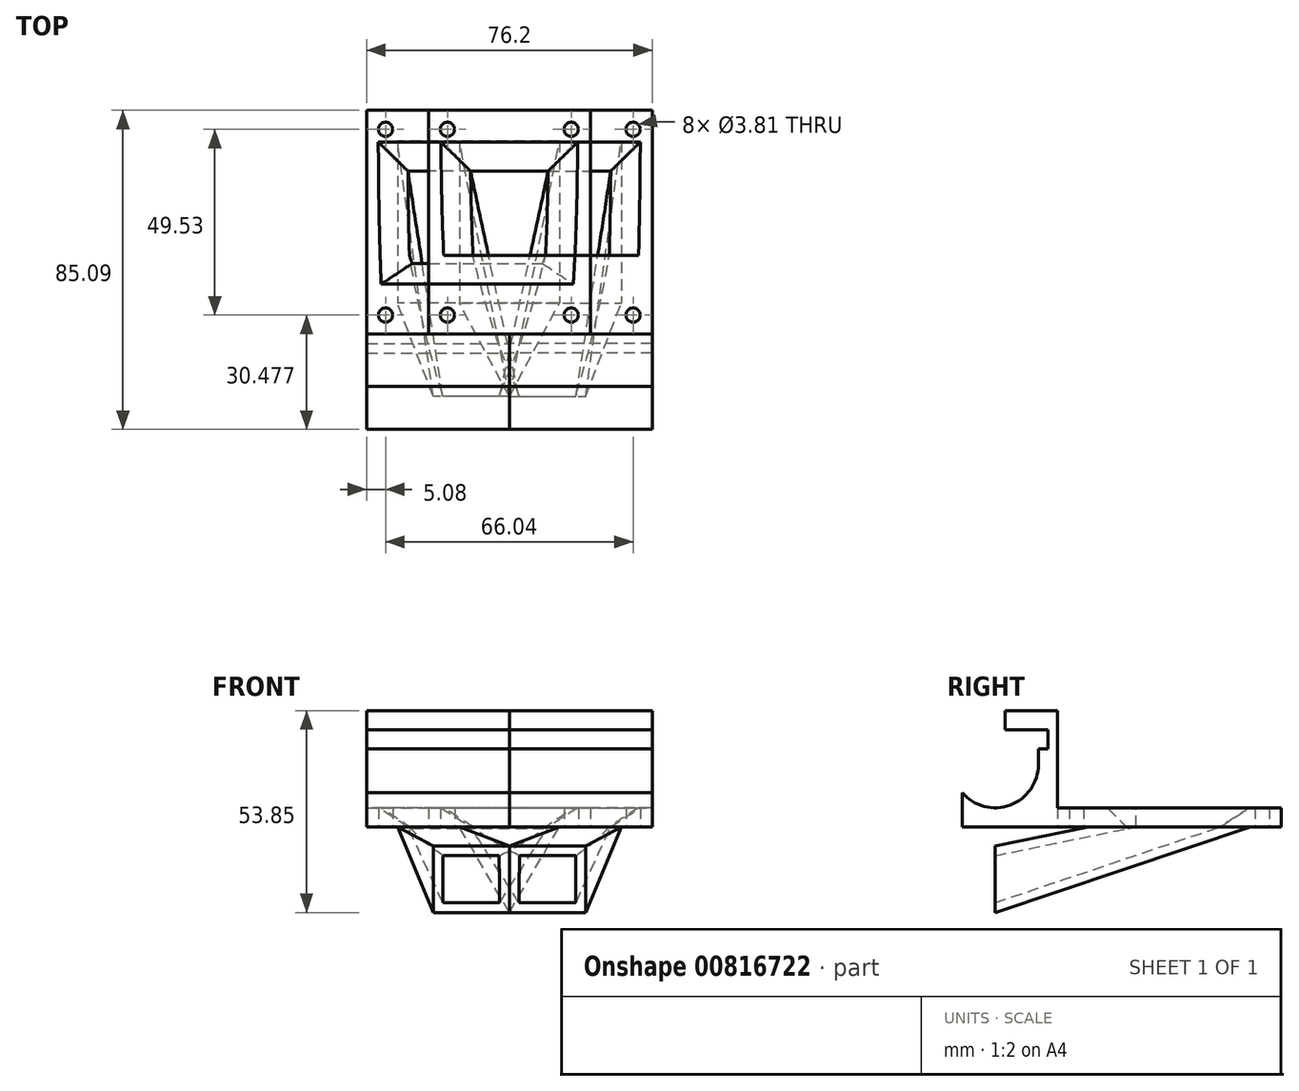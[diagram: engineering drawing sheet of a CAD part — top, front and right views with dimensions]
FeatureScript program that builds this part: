
annotation { "Feature Type Name" : "Feature", "Feature Type Description" : "" }
export const myFeature = defineFeature(function(context is Context, id is Id, definition is map)
    precondition{}
    {
        {
            var Q0;
            Q0=qCreatedBy(makeId("Right.planeOp"),FACE);
            var sketch = newSketch(context, id + "F0", { "sketchPlane" : qUnion([Q0])});
            skArc(sketch, "E0", {"start": v(-8.76, -7.53) * mm, "mid": v(4.02, -10.84) * mm, "end": v(11.56, 0) * mm});
            skLineSegment(sketch, "E1", {"start": v(-8.76, -7.53) * mm, "end": v(-8.76, -16.64) * mm});
            skLineSegment(sketch, "E2", {"start": v(-8.76, -16.64) * mm, "end": v(11.56, -16.64) * mm});
            skLineSegment(sketch, "E3", {"start": v(11.56, 0) * mm, "end": v(11.56, 4.2) * mm});
            skLineSegment(sketch, "E4", {"start": v(11.56, 4.2) * mm, "end": v(14.1, 4.2) * mm});
            skLineSegment(sketch, "E5", {"start": v(14.1, 4.2) * mm, "end": v(14.1, 9.27) * mm});
            skLineSegment(sketch, "E6", {"start": v(14.1, 9.27) * mm, "end": v(11.56, 9.27) * mm});
            skLineSegment(sketch, "E7", {"start": v(11.56, 9.27) * mm, "end": v(2.67, 9.27) * mm});
            skLineSegment(sketch, "E8", {"start": v(2.67, 9.27) * mm, "end": v(2.67, 14.35) * mm});
            skLineSegment(sketch, "E9", {"start": v(2.67, 14.35) * mm, "end": v(16.64, 14.35) * mm});
            skLineSegment(sketch, "E10", {"start": v(16.64, 14.35) * mm, "end": v(16.64, -16.64) * mm});
            skLineSegment(sketch, "E11", {"start": v(16.64, -16.64) * mm, "end": v(11.56, -16.64) * mm});
            skSolve(sketch);
        }
        {
            var Q0;
            Q0=makeQuery(id+"F0.imprint","IMPRINT",FACE,{"disambiguationData":[TD([[makeQuery(id+"F0.imprint","IMPRINT",EDGE,{"derivedFrom":sQuery(id+"F0.wireOp",EDGE,"E0")}),-1.0]])]});
            extrude(context, id + "F1", {"entities" : qUnion([Q0]), "depth" : 38.1 * mm, "offsetDistance" : 25.4 * mm});
        }
        {
            var Q0;
            Q0=makeQuery(id+"F1.opExtrude","SWEPT_FACE",FACE,{"disambiguationData":[OSD([sQuery(id+"F0.wireOp",EDGE,"E2"),sQuery(id+"F0.wireOp",EDGE,"E11")])]});
            var sketch = newSketch(context, id + "F2", { "sketchPlane" : qUnion([Q0])});
            skLineSegment(sketch, "E12", {"start": v(0, -16.64) * mm, "end": v(-21.6, -16.64) * mm});
            skLineSegment(sketch, "E13", {"start": v(-21.6, -16.64) * mm, "end": v(-21.59, -76.33) * mm});
            skLineSegment(sketch, "E14", {"start": v(-21.59, -76.33) * mm, "end": v(38.1, -76.33) * mm});
            skLineSegment(sketch, "E15", {"start": v(38.1, -76.33) * mm, "end": v(38.1, -16.64) * mm});
            skCircle(sketch, "E16", {"center": v(33.02, -71.25) * mm, "radius": 1.9 * mm});
            skCircle(sketch, "E17.0.1.0", {"center": v(33.02, -21.72) * mm, "radius": 1.9 * mm});
            skCircle(sketch, "E17.1.0.0", {"center": v(-16.51, -71.25) * mm, "radius": 1.9 * mm});
            skCircle(sketch, "E17.1.1.0", {"center": v(-16.51, -21.72) * mm, "radius": 1.9 * mm});
            skLineSegment(sketch, "E17.direction1", {"start": v(33.02, -71.25) * mm, "end": v(-16.51, -71.25) * mm, "construction": true});
            skLineSegment(sketch, "E17.direction2", {"start": v(33.02, -71.25) * mm, "end": v(33.02, -21.72) * mm, "construction": true});
            skPoint(sketch, "E18.top.end.orphan", {"position": v(0, -24.9) * mm});
            skLineSegment(sketch, "E19.bottom", {"start": v(-13.33, -68.07) * mm, "end": v(29.85, -68.07) * mm});
            skLineSegment(sketch, "E19.top", {"start": v(-13.34, -24.9) * mm, "end": v(29.84, -24.9) * mm});
            skLineSegment(sketch, "E19.left", {"start": v(-13.33, -68.07) * mm, "end": v(-13.34, -24.9) * mm});
            skLineSegment(sketch, "E19.right", {"start": v(29.85, -68.07) * mm, "end": v(29.84, -24.9) * mm});
            skSolve(sketch);
        }
        {
            var Q0;
            Q0=makeQuery(id+"F2.imprint","IMPRINT",FACE,{"disambiguationData":[TD([[makeQuery(id+"F2.imprint","IMPRINT",EDGE,{"derivedFrom":sQuery(id+"F2.wireOp",EDGE,"E12")}),1.0]])]});
            extrude(context, id + "F3", {"entities" : qUnion([Q0]), "operationType" : NewBodyOperationType.ADD, "oppositeDirection" : true, "depth" : 5.08 * mm, "offsetDistance" : 25.4 * mm});
        }
        {
            var Q0;
            Q0=qCreatedBy(makeId("Front.planeOp"),FACE);
            var sketch = newSketch(context, id + "F4", { "sketchPlane" : qUnion([Q0])});
            skLineSegment(sketch, "E20.bottom", {"start": v(0, -21.72) * mm, "end": v(20.32, -21.72) * mm});
            skLineSegment(sketch, "E20.top", {"start": v(0, -39.5) * mm, "end": v(20.32, -39.5) * mm});
            skLineSegment(sketch, "E20.left", {"start": v(0, -21.72) * mm, "end": v(0, -39.5) * mm});
            skLineSegment(sketch, "E20.right", {"start": v(20.32, -21.72) * mm, "end": v(20.32, -39.5) * mm});
            skSolve(sketch);
        }
        {
            var Q0;
            {var subQ0=sQuery(id+"F0.wireOp",EDGE,"E11");Q0=makeQuery(id+"F3.boolean.opBoolean","MERGE",FACE,{"derivedFrom":[makeQuery(id+"F1.opExtrude","SWEPT_FACE",FACE,{"disambiguationData":[OSD([sQuery(id+"F0.wireOp",EDGE,"E2"),subQ0])]}),makeQuery(id+"F3.opExtrude","CAP_FACE",FACE,{"disambiguationData":[OSD([sQuery(id+"F0.wireOp",EDGE,"E10"),subQ0,sQuery(id+"F2.wireOp",EDGE,"E12"),sQuery(id+"F2.wireOp",EDGE,"E13"),sQuery(id+"F2.wireOp",EDGE,"E14"),sQuery(id+"F2.wireOp",EDGE,"E15"),sQuery(id+"F2.wireOp",EDGE,"E16"),sQuery(id+"F2.wireOp",EDGE,"E17.0.1.0"),sQuery(id+"F2.wireOp",EDGE,"E17.1.0.0"),sQuery(id+"F2.wireOp",EDGE,"E17.1.1.0"),sQuery(id+"F2.wireOp",EDGE,"E19.bottom"),sQuery(id+"F2.wireOp",EDGE,"E19.top"),sQuery(id+"F2.wireOp",EDGE,"E19.left"),sQuery(id+"F2.wireOp",EDGE,"E19.right")])],"isStart":true})]});}
            var sketch = newSketch(context, id + "F5", { "sketchPlane" : qUnion([Q0])});
            skLineSegment(sketch, "E21.bottom", {"start": v(-24.13, -14.1) * mm, "end": v(40.64, -14.1) * mm});
            skLineSegment(sketch, "E21.top", {"start": v(-24.13, -78.87) * mm, "end": v(40.64, -78.87) * mm});
            skLineSegment(sketch, "E21.left", {"start": v(-24.13, -14.1) * mm, "end": v(-24.13, -78.87) * mm});
            skLineSegment(sketch, "E21.right", {"start": v(40.64, -14.1) * mm, "end": v(40.64, -78.87) * mm});
            skSolve(sketch);
        }
        {
            var Q0;
            Q0=makeQuery(id+"F4.imprint","IMPRINT",FACE,{"disambiguationData":[TD([[makeQuery(id+"F4.imprint","IMPRINT",EDGE,{"derivedFrom":sQuery(id+"F4.wireOp",EDGE,"E20.bottom")}),-1.0]])]});
            var Q1;
            Q1=makeQuery(id+"F5.imprint","IMPRINT",FACE,{"disambiguationData":[TD([[makeQuery(id+"F5.imprint","IMPRINT",EDGE,{"derivedFrom":makeQuery(id+"F3.opExtrude","CAP_EDGE",EDGE,{"disambiguationData":[OSD([sQuery(id+"F2.wireOp",EDGE,"E19.bottom")])],"isStart":true})}),1.0]])]});
            loft(context, id + "F6", {"sheetProfilesArray" : [{ "sheetProfileEntities" : qUnion([Q0]) }, { "sheetProfileEntities" : qUnion([Q1]) }]});
        }
        {
            var Q0;
            Q0=makeQuery(id+"F6.opLoft","CAP_FACE",FACE,{"disambiguationData":[OSD([makeQuery(id+"F5.imprint","IMPRINT",FACE,{"disambiguationData":[TD([[makeQuery(id+"F5.imprint","IMPRINT",EDGE,{"derivedFrom":makeQuery(id+"F3.opExtrude","CAP_EDGE",EDGE,{"disambiguationData":[OSD([sQuery(id+"F2.wireOp",EDGE,"E19.bottom")])],"isStart":true})}),1.0]])]})])],"isStart":true});
            var Q1;
            Q1=makeQuery(id+"F6.opLoft","CAP_FACE",FACE,{"disambiguationData":[OSD([makeQuery(id+"F4.imprint","IMPRINT",FACE,{"disambiguationData":[TD([[makeQuery(id+"F4.imprint","IMPRINT",EDGE,{"derivedFrom":sQuery(id+"F4.wireOp",EDGE,"E20.bottom")}),-1.0]])]})])],"isStart":true});
            shell(context, id + "F7", {"entities" : qUnion([Q0, Q1]), "thickness" : 2.54 * mm});
        }
        {
            var Q0;
            Q0=makeQuery(id+"F6.opLoft","CAP_FACE",FACE,{"disambiguationData":[OSD([makeQuery(id+"F5.imprint","IMPRINT",FACE,{"disambiguationData":[TD([[makeQuery(id+"F5.imprint","IMPRINT",EDGE,{"derivedFrom":makeQuery(id+"F3.opExtrude","CAP_EDGE",EDGE,{"disambiguationData":[OSD([sQuery(id+"F2.wireOp",EDGE,"E19.bottom")])],"isStart":true})}),1.0]])]})])],"isStart":true});
            extrude(context, id + "F8", {"entities" : qUnion([Q0]), "operationType" : NewBodyOperationType.ADD, "depth" : 5.08 * mm, "offsetDistance" : 25.4 * mm});
        }
        {
            var Q0;
            {var subQ0=sQuery(id+"F2.wireOp",EDGE,"E19.left");var subQ1=sQuery(id+"F2.wireOp",EDGE,"E19.top");var subQ2=sQuery(id+"F2.wireOp",EDGE,"E19.bottom");Q0=makeQuery(id+"F8.opExtrude","CAP_EDGE",EDGE,{"disambiguationData":[OSD([subQ2,subQ1,subQ0]),TDD([makeQuery(id+"F7.opShell","OFFSET_EDGE",EDGE,{"disambiguationData":[OSD([subQ2,subQ1,subQ0])]})])],"isStart":false});}
            var Q1;
            {var subQ0=sQuery(id+"F2.wireOp",EDGE,"E19.right");var subQ1=sQuery(id+"F2.wireOp",EDGE,"E19.left");var subQ2=sQuery(id+"F2.wireOp",EDGE,"E19.bottom");Q1=makeQuery(id+"F8.opExtrude","CAP_EDGE",EDGE,{"disambiguationData":[OSD([subQ2,subQ1,subQ0]),TDD([makeQuery(id+"F7.opShell","OFFSET_EDGE",EDGE,{"disambiguationData":[OSD([subQ2,subQ1,subQ0])]})])],"isStart":false});}
            var Q2;
            {var subQ0=sQuery(id+"F2.wireOp",EDGE,"E19.right");var subQ1=sQuery(id+"F2.wireOp",EDGE,"E19.top");var subQ2=sQuery(id+"F2.wireOp",EDGE,"E19.bottom");Q2=makeQuery(id+"F8.opExtrude","CAP_EDGE",EDGE,{"disambiguationData":[OSD([subQ2,subQ1,subQ0]),TDD([makeQuery(id+"F7.opShell","OFFSET_EDGE",EDGE,{"disambiguationData":[OSD([subQ2,subQ1,subQ0])]})])],"isStart":false});}
            chamfer(context, id + "F9", {"entities" : qUnion([Q0, Q1, Q2]), "chamferType" : ChamferType.OFFSET_ANGLE, "width" : 5.08 * mm, "oppositeDirection" : false, "angle" : 57 * degree, "tangentPropagation" : true});
        }
        {
            var Q0;
            Q0=makeQuery(id+"F1.opExtrude","SWEPT_BODY",BODY,{"disambiguationData":[OSD([sQuery(id+"F0.wireOp",EDGE,"E0"),sQuery(id+"F0.wireOp",EDGE,"E1"),sQuery(id+"F0.wireOp",EDGE,"E2"),sQuery(id+"F0.wireOp",EDGE,"E3"),sQuery(id+"F0.wireOp",EDGE,"E4"),sQuery(id+"F0.wireOp",EDGE,"E5"),sQuery(id+"F0.wireOp",EDGE,"E6"),sQuery(id+"F0.wireOp",EDGE,"E7"),sQuery(id+"F0.wireOp",EDGE,"E8"),sQuery(id+"F0.wireOp",EDGE,"E9"),sQuery(id+"F0.wireOp",EDGE,"E10"),sQuery(id+"F0.wireOp",EDGE,"E11")])]});
            var Q1;
            Q1=qCreatedBy(makeId("Right.planeOp"),FACE);
            mirror(context, id + "F10", {"entities" : qUnion([Q0]), "mirrorPlane" : qUnion([Q1])});
        }
        {
            var Q0;
            {var subQ0=sQuery(id+"F2.wireOp",EDGE,"E19.right");var subQ1=sQuery(id+"F2.wireOp",EDGE,"E19.left");var subQ2=sQuery(id+"F2.wireOp",EDGE,"E19.top");Q0=makeQuery(id+"F10.opPattern","COPY",EDGE,{"derivedFrom":makeQuery(id+"F8.opExtrude","CAP_EDGE",EDGE,{"disambiguationData":[OSD([subQ2,subQ1,subQ0]),TDD([makeQuery(id+"F7.opShell","OFFSET_EDGE",EDGE,{"disambiguationData":[OSD([subQ2,subQ1,subQ0])]})])],"isStart":false}),"instanceName":"1"});}
            chamfer(context, id + "F11", {"entities" : qUnion([Q0]), "width" : 7.62 * mm, "tangentPropagation" : true});
        }
    });
